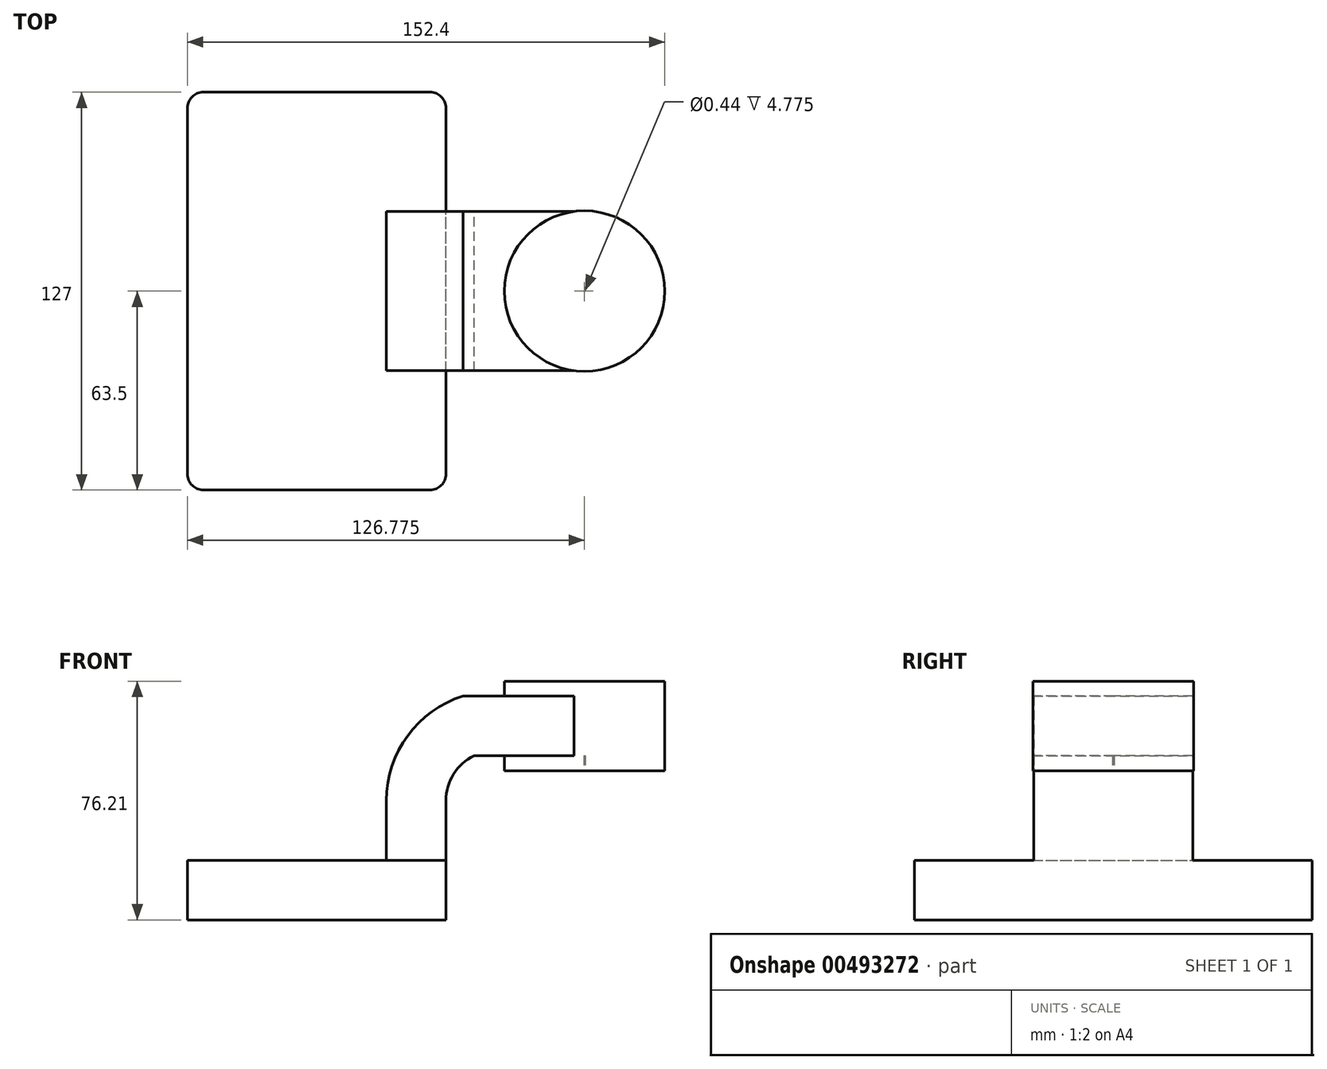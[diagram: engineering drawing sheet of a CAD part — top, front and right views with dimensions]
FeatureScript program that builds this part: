
annotation { "Feature Type Name" : "Feature", "Feature Type Description" : "" }
export const myFeature = defineFeature(function(context is Context, id is Id, definition is map)
    precondition{}
    {
        {
            var Q0;
            Q0=qCreatedBy(makeId("Front.planeOp"),FACE);
            var sketch = newSketch(context, id + "F0", { "sketchPlane" : qUnion([Q0])});
            skLineSegment(sketch, "E0.bottom", {"start": v(41.27, 9.53) * mm, "end": v(-41.28, 9.53) * mm});
            skLineSegment(sketch, "E0.top", {"start": v(41.28, -9.52) * mm, "end": v(-41.28, -9.53) * mm});
            skLineSegment(sketch, "E0.left", {"start": v(41.28, 9.53) * mm, "end": v(41.28, -9.52) * mm});
            skLineSegment(sketch, "E0.right", {"start": v(-41.28, 9.53) * mm, "end": v(-41.28, -9.53) * mm});
            skPoint(sketch, "E0.middle", {"position": v(0, 0) * mm});
            skLineSegment(sketch, "E1.bottom", {"start": v(111.12, 66.68) * mm, "end": v(60.33, 66.68) * mm});
            skLineSegment(sketch, "E1.top", {"start": v(111.12, 38.1) * mm, "end": v(60.33, 38.1) * mm});
            skLineSegment(sketch, "E1.left", {"start": v(111.12, 66.68) * mm, "end": v(111.12, 38.1) * mm});
            skLineSegment(sketch, "E1.right", {"start": v(60.33, 66.68) * mm, "end": v(60.33, 38.1) * mm});
            skPoint(sketch, "E1.middle", {"position": v(85.72, 52.39) * mm});
            skLineSegment(sketch, "E2", {"start": v(41.27, 9.53) * mm, "end": v(41.27, 28.58) * mm});
            skArc(sketch, "E3", {"start": v(41.27, 28.58) * mm, "mid": v(43.7, 37.02) * mm, "end": v(50.26, 42.88) * mm});
            skLineSegment(sketch, "E4", {"start": v(50.26, 42.88) * mm, "end": v(85.72, 42.88) * mm});
            skLineSegment(sketch, "E5.0", {"start": v(46.78, 61.93) * mm, "end": v(85.72, 61.93) * mm});
            skArc(sketch, "E5.1", {"start": v(22.23, 28.58) * mm, "mid": v(29.03, 49.28) * mm, "end": v(46.78, 61.93) * mm});
            skLineSegment(sketch, "E5.2", {"start": v(22.22, 9.53) * mm, "end": v(22.22, 28.58) * mm});
            skLineSegment(sketch, "E6", {"start": v(85.72, 52.39) * mm, "end": v(85.72, 38.1) * mm});
            skLineSegment(sketch, "E7", {"start": v(85.5, 38.52) * mm, "end": v(85.5, 66.68) * mm});
            skFitSpline(sketch, "E8", {"points": [v(-41.28, 9.52) * mm, v(46.78, 61.93) * mm], "startDerivative": vector(3.24, 89.52) * mm, "endDerivative": vector(96.21, 2.12) * mm});
            skSolve(sketch);
        }
        {
            var Q0;
            Q0=makeQuery(id+"F0.imprint","IMPRINT",FACE,{"disambiguationData":[TD([[makeQuery(id+"F0.imprint","IMPRINT",EDGE,{"derivedFrom":sQuery(id+"F0.wireOp",EDGE,"E0.top")}),-1.0]])]});
            extrude(context, id + "F1", {"entities" : qUnion([Q0]), "endBound" : BoundingType.SYMMETRIC, "depth" : 127 * mm});
        }
        {
            var Q0;
            {var subQ1=sQuery(id+"F0.wireOp",EDGE,"E2");Q0=makeQuery(id+"F0.imprint","IMPRINT",FACE,{"disambiguationData":[TD([[makeQuery(id+"F0.imprint","IMPRINT",EDGE,{"derivedFrom":subQ1}),1.0]])]});}
            var Q1;
            {var subQ0=sQuery(id+"F0.wireOp",EDGE,"E5.0");var subQ1=sQuery(id+"F0.wireOp",EDGE,"E1.right");var subQ2=makeQuery(id+"F0.imprint","INTERSECT",VERTEX,{"derivedFrom":[subQ1,subQ0]});Q1=makeQuery(id+"F0.imprint","IMPRINT",FACE,{"disambiguationData":[TD([[makeQuery(id+"F0.imprint","IMPRINT",EDGE,{"disambiguationData":[TD([[subQ2,-1.0]])],"derivedFrom":subQ1}),1.0]])]});}
            extrude(context, id + "F2", {"entities" : qUnion([Q0, Q1]), "operationType" : NewBodyOperationType.ADD, "endBound" : BoundingType.SYMMETRIC, "depth" : 50.8 * mm});
        }
        {
            var Q0;
            Q0=makeQuery(id+"F0.imprint","IMPRINT",FACE,{"disambiguationData":[TD([[makeQuery(id+"F0.imprint","IMPRINT",EDGE,{"derivedFrom":sQuery(id+"F0.wireOp",EDGE,"E5.1")}),1.0]])]});
            extrude(context, id + "F3", {"entities" : qUnion([Q0]), "operationType" : NewBodyOperationType.ADD, "endBound" : BoundingType.SYMMETRIC, "depth" : 15.88 * mm});
        }
        {
            var Q0;
            {var subQ0=sQuery(id+"F0.wireOp",EDGE,"E1.left");Q0=makeQuery(id+"F0.imprint","IMPRINT",FACE,{"disambiguationData":[TD([[makeQuery(id+"F0.imprint","IMPRINT",EDGE,{"derivedFrom":subQ0}),-1.0]])]});}
            var Q1;
            Q1=sQuery(id+"F0.wireOp",EDGE,"E7");
            revolve(context, id + "F4", {"operationType" : NewBodyOperationType.ADD, "entities" : qUnion([Q0]), "axis" : qUnion([Q1]), "revolveType" : RevolveType.FULL});
        }
        {
            var Q0;
            Q0=makeQuery(id+"F1.opExtrude","CAP_EDGE",EDGE,{"disambiguationData":[OSD([sQuery(id+"F0.wireOp",EDGE,"E0.right")])],"isStart":false});
            var Q1;
            Q1=makeQuery(id+"F1.opExtrude","CAP_EDGE",EDGE,{"disambiguationData":[OSD([sQuery(id+"F0.wireOp",EDGE,"E0.left")])],"isStart":false});
            var Q2;
            Q2=makeQuery(id+"F1.opExtrude","CAP_EDGE",EDGE,{"disambiguationData":[OSD([sQuery(id+"F0.wireOp",EDGE,"E0.left")])],"isStart":true});
            var Q3;
            Q3=makeQuery(id+"F1.opExtrude","CAP_EDGE",EDGE,{"disambiguationData":[OSD([sQuery(id+"F0.wireOp",EDGE,"E0.right")])],"isStart":true});
            fillet(context, id + "F5", {"entities" : qUnion([Q0, Q1, Q2, Q3]), "radius" : 5.08 * mm, "tangentPropagation" : true, "allowEdgeOverflow" : false});
        }
    });
